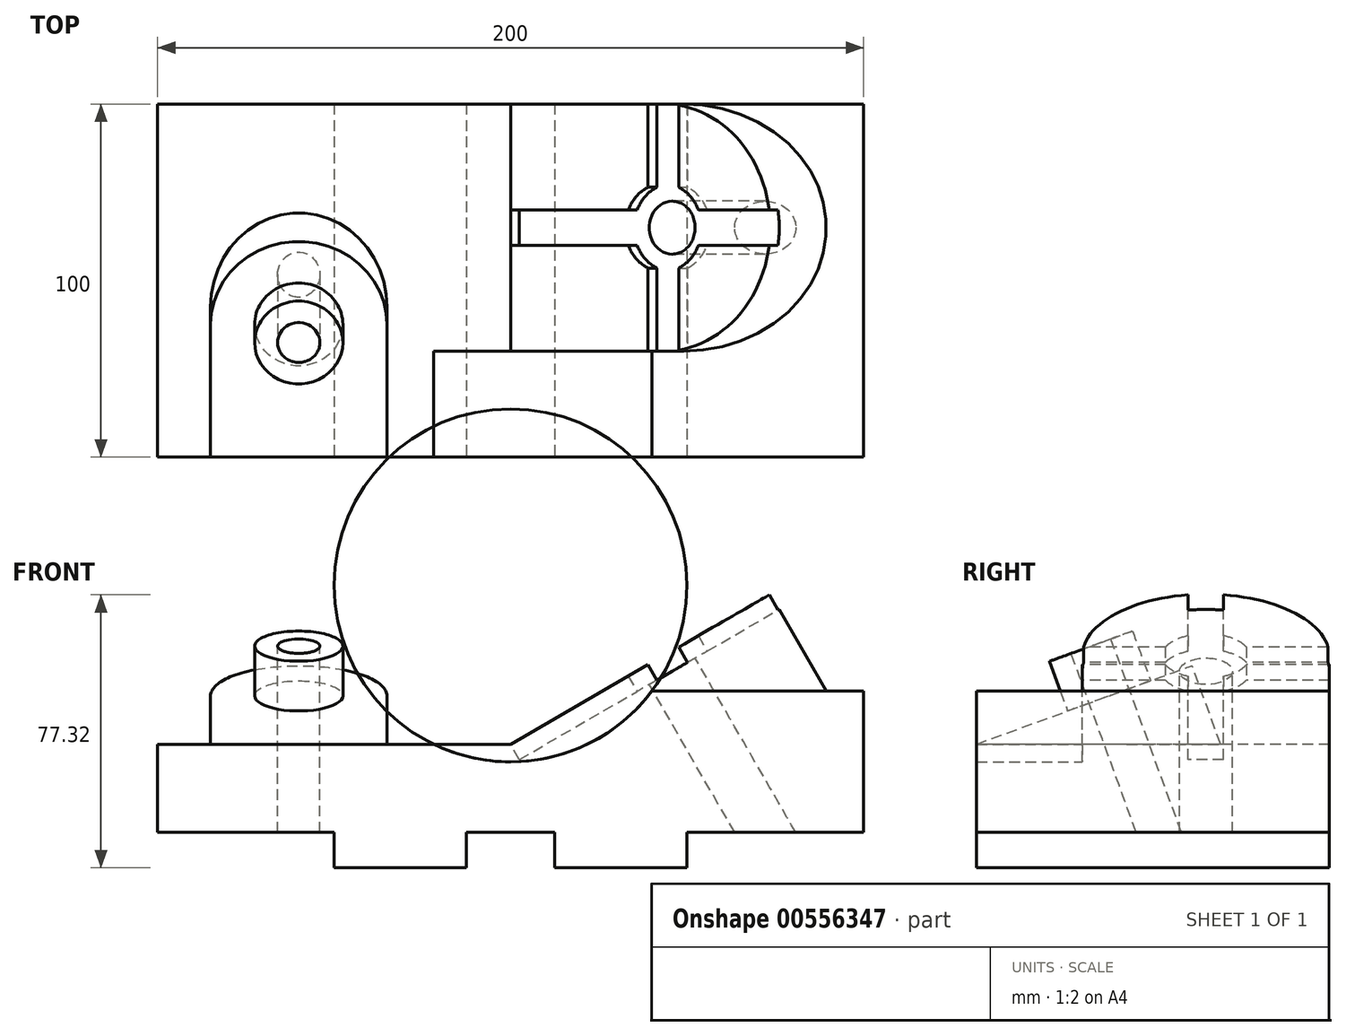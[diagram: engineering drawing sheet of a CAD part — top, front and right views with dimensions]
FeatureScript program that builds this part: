
annotation { "Feature Type Name" : "Feature", "Feature Type Description" : "" }
export const myFeature = defineFeature(function(context is Context, id is Id, definition is map)
    precondition{}
    {
        {
            var Q0;
            Q0=qCreatedBy(makeId("Front.planeOp"),FACE);
            var sketch = newSketch(context, id + "F0", { "sketchPlane" : qUnion([Q0])});
            skLineSegment(sketch, "E0", {"start": v(-200, 35) * mm, "end": v(-200, 10) * mm});
            skLineSegment(sketch, "E1", {"start": v(-200, 10) * mm, "end": v(-150, 10) * mm});
            skLineSegment(sketch, "E2", {"start": v(-150, 10) * mm, "end": v(-150, 0) * mm});
            skLineSegment(sketch, "E3", {"start": v(-150, 0) * mm, "end": v(-112.5, 0) * mm});
            skLineSegment(sketch, "E4", {"start": v(-112.5, 0) * mm, "end": v(-112.5, 10) * mm});
            skLineSegment(sketch, "E5", {"start": v(-112.5, 10) * mm, "end": v(-87.5, 10) * mm});
            skLineSegment(sketch, "E6", {"start": v(-87.5, 10) * mm, "end": v(-87.5, 0) * mm});
            skLineSegment(sketch, "E7", {"start": v(-87.5, 0) * mm, "end": v(-50, 0) * mm});
            skLineSegment(sketch, "E8", {"start": v(-50, 0) * mm, "end": v(-50, 10) * mm});
            skLineSegment(sketch, "E9", {"start": v(-50, 10) * mm, "end": v(0, 10) * mm});
            skLineSegment(sketch, "E10", {"start": v(0, 10) * mm, "end": v(0, 50) * mm});
            skLineSegment(sketch, "E11", {"start": v(-200, 35) * mm, "end": v(-100, 35) * mm});
            skLineSegment(sketch, "E12", {"start": v(-100, 35) * mm, "end": v(-60, 50) * mm});
            skLineSegment(sketch, "E13", {"start": v(-60, 50) * mm, "end": v(0, 50) * mm});
            skSolve(sketch);
        }
        {
            var Q0;
            Q0 = qSketchRegion(id + "F0", true);
            extrude(context, id + "F1", {"entities" : qUnion([Q0]), "oppositeDirection" : true, "depth" : 100 * mm, "offsetDistance" : 25 * mm});
        }
        {
            var Q0;
            Q0=makeQuery(id+"F1.opExtrude","CAP_EDGE",EDGE,{"disambiguationData":[OSD([sQuery(id+"F0.wireOp",EDGE,"E11")])],"isStart":true});
            var Q1;
            Q1=makeQuery(id+"F1.opExtrude","SWEPT_FACE",FACE,{"disambiguationData":[OSD([sQuery(id+"F0.wireOp",EDGE,"E11")])]});
            cPlane(context, id + "F2", {"entities" : qUnion([Q0, Q1]), "cplaneType" : CPlaneType.LINE_ANGLE, "offset" : 25 * mm, "angle" : 20 * degree, "width" : 150 * mm, "height" : 150 * mm});
        }
        {
            var Q0;
            Q0=qCreatedBy(id+"F2.planeOp",FACE);
            var sketch = newSketch(context, id + "F3", { "sketchPlane" : qUnion([Q0])});
            skLineSegment(sketch, "E14", {"start": v(-135, -11.97) * mm, "end": v(-135, -51.97) * mm});
            skLineSegment(sketch, "E15", {"start": v(-185, -51.97) * mm, "end": v(-185, -11.97) * mm});
            skLineSegment(sketch, "E16", {"start": v(-185, -11.97) * mm, "end": v(-135, -11.97) * mm});
            skArc(sketch, "E17", {"start": v(-135, -51.97) * mm, "mid": v(-160, -76.97) * mm, "end": v(-185, -51.97) * mm});
            skSolve(sketch);
        }
        {
            var Q0;
            Q0 = qSketchRegion(id + "F3", true);
            var Q1;
            Q1=makeQuery(id+"F1.opExtrude","SWEPT_BODY",BODY,{"disambiguationData":[OSD([sQuery(id+"F0.wireOp",EDGE,"E0"),sQuery(id+"F0.wireOp",EDGE,"E1"),sQuery(id+"F0.wireOp",EDGE,"E2"),sQuery(id+"F0.wireOp",EDGE,"E3"),sQuery(id+"F0.wireOp",EDGE,"E4"),sQuery(id+"F0.wireOp",EDGE,"E5"),sQuery(id+"F0.wireOp",EDGE,"E6"),sQuery(id+"F0.wireOp",EDGE,"E7"),sQuery(id+"F0.wireOp",EDGE,"E8"),sQuery(id+"F0.wireOp",EDGE,"E9"),sQuery(id+"F0.wireOp",EDGE,"E10"),sQuery(id+"F0.wireOp",EDGE,"E11"),sQuery(id+"F0.wireOp",EDGE,"E12"),sQuery(id+"F0.wireOp",EDGE,"E13")])]});
            extrude(context, id + "F4", {"entities" : qUnion([Q0]), "operationType" : NewBodyOperationType.ADD, "endBound" : BoundingType.UP_TO_BODY, "depth" : 25 * mm, "endBoundEntityBody" : qUnion([Q1]), "offsetDistance" : 25 * mm});
        }
        {
            var Q0;
            Q0=qCreatedBy(id+"F2.planeOp",FACE);
            var sketch = newSketch(context, id + "F5", { "sketchPlane" : qUnion([Q0])});
            skCircle(sketch, "E18", {"center": v(-160, -51.97) * mm, "radius": 12.5 * mm});
            skSolve(sketch);
        }
        {
            var Q0;
            Q0 = qSketchRegion(id + "F5", true);
            extrude(context, id + "F6", {"entities" : qUnion([Q0]), "operationType" : NewBodyOperationType.ADD, "oppositeDirection" : true, "depth" : 15 * mm, "offsetDistance" : 25 * mm});
        }
        {
            var Q0;
            Q0=makeQuery(id+"F6.opExtrude","CAP_FACE",FACE,{"disambiguationData":[OSD([sQuery(id+"F5.wireOp",EDGE,"E18")])],"isStart":false});
            var sketch = newSketch(context, id + "F7", { "sketchPlane" : qUnion([Q0])});
            skCircle(sketch, "E19", {"center": v(-160, 51.97) * mm, "radius": 6 * mm});
            skSolve(sketch);
        }
        {
            var Q0;
            Q0 = qSketchRegion(id + "F7", true);
            extrude(context, id + "F8", {"entities" : qUnion([Q0]), "operationType" : NewBodyOperationType.REMOVE, "endBound" : BoundingType.THROUGH_ALL, "oppositeDirection" : true, "depth" : 25 * mm, "offsetDistance" : 25 * mm});
        }
        {
            var Q0;
            Q0=makeQuery(id+"F1.opExtrude","SWEPT_EDGE",EDGE,{"disambiguationData":[OSD([sQuery(id+"F0.wireOp",EDGE,"E11"),sQuery(id+"F0.wireOp",EDGE,"E12")])]});
            var Q1;
            Q1=makeQuery(id+"F1.opExtrude","SWEPT_FACE",FACE,{"disambiguationData":[OSD([sQuery(id+"F0.wireOp",EDGE,"E11")])]});
            cPlane(context, id + "F9", {"entities" : qUnion([Q0, Q1]), "cplaneType" : CPlaneType.LINE_ANGLE, "offset" : 25 * mm, "angle" : 30 * degree, "width" : 150 * mm, "height" : 150 * mm});
        }
        {
            var Q0;
            Q0=qCreatedBy(id+"F9.planeOp",FACE);
            var sketch = newSketch(context, id + "F10", { "sketchPlane" : qUnion([Q0])});
            skLineSegment(sketch, "E20", {"start": v(-69.1, -30) * mm, "end": v(-69.1, -100) * mm});
            skLineSegment(sketch, "E21", {"start": v(-69.1, -100) * mm, "end": v(-19.1, -100) * mm});
            skArc(sketch, "E22", {"start": v(-19.1, -100) * mm, "mid": v(15.9, -65) * mm, "end": v(-19.1, -30) * mm});
            skLineSegment(sketch, "E23", {"start": v(-69.1, -30) * mm, "end": v(-19.1, -30) * mm});
            skSolve(sketch);
        }
        {
            var Q0;
            Q0 = qSketchRegion(id + "F10", true);
            var Q1;
            Q1=makeQuery(id+"F1.opExtrude","SWEPT_BODY",BODY,{"disambiguationData":[OSD([sQuery(id+"F0.wireOp",EDGE,"E0"),sQuery(id+"F0.wireOp",EDGE,"E1"),sQuery(id+"F0.wireOp",EDGE,"E2"),sQuery(id+"F0.wireOp",EDGE,"E3"),sQuery(id+"F0.wireOp",EDGE,"E4"),sQuery(id+"F0.wireOp",EDGE,"E5"),sQuery(id+"F0.wireOp",EDGE,"E6"),sQuery(id+"F0.wireOp",EDGE,"E7"),sQuery(id+"F0.wireOp",EDGE,"E8"),sQuery(id+"F0.wireOp",EDGE,"E9"),sQuery(id+"F0.wireOp",EDGE,"E10"),sQuery(id+"F0.wireOp",EDGE,"E11"),sQuery(id+"F0.wireOp",EDGE,"E12"),sQuery(id+"F0.wireOp",EDGE,"E13")])]});
            extrude(context, id + "F11", {"entities" : qUnion([Q0]), "operationType" : NewBodyOperationType.ADD, "endBound" : BoundingType.UP_TO_BODY, "depth" : 25 * mm, "endBoundEntityBody" : qUnion([Q1]), "offsetDistance" : 25 * mm});
        }
        {
            var Q0;
            Q0=makeQuery(id+"F11.opExtrude","SWEPT_FACE",FACE,{"disambiguationData":[OSD([sQuery(id+"F10.wireOp",EDGE,"E23")])]});
            var sketch = newSketch(context, id + "F12", { "sketchPlane" : qUnion([Q0])});
            skArc(sketch, "E24", {"start": v(-130.65, 40.5) * mm, "mid": v(-64.98, 44.31) * mm, "end": v(-59.92, 109.9) * mm});
            skLineSegment(sketch, "E25", {"start": v(-100, 80) * mm, "end": v(-100, 35) * mm, "construction": true});
            skLineSegment(sketch, "E26", {"start": v(-100, 35) * mm, "end": v(-100, 30) * mm, "construction": true});
            skLineSegment(sketch, "E27", {"start": v(-130.65, 40.5) * mm, "end": v(-59.92, 109.9) * mm});
            skSolve(sketch);
        }
        {
            var Q0;
            Q0 = qSketchRegion(id + "F12", true);
            extrude(context, id + "F13", {"entities" : qUnion([Q0]), "operationType" : NewBodyOperationType.REMOVE, "endBound" : BoundingType.THROUGH_ALL, "depth" : 25 * mm, "offsetDistance" : 25 * mm});
        }
        {
            var Q0;
            Q0=qCreatedBy(id+"F9.planeOp",FACE);
            var sketch = newSketch(context, id + "F14", { "sketchPlane" : qUnion([Q0])});
            skLineSegment(sketch, "E28.bottom", {"start": v(-24.1, -100) * mm, "end": v(-14.1, -100) * mm});
            skLineSegment(sketch, "E28.top", {"start": v(-24.1, -30) * mm, "end": v(-14.1, -30) * mm});
            skLineSegment(sketch, "E28.left", {"start": v(-24.1, -100) * mm, "end": v(-24.1, -70) * mm});
            skLineSegment(sketch, "E28.right", {"start": v(-14.1, -100) * mm, "end": v(-14.1, -70) * mm});
            skLineSegment(sketch, "E29.bottom", {"start": v(-69.1, -70) * mm, "end": v(-24.1, -70) * mm});
            skLineSegment(sketch, "E29.top", {"start": v(-69.1, -60) * mm, "end": v(-24.1, -60) * mm});
            skLineSegment(sketch, "E29.left", {"start": v(-69.1, -70) * mm, "end": v(-69.1, -60) * mm});
            skLineSegment(sketch, "E29.right", {"start": v(56.23, -70) * mm, "end": v(56.23, -60) * mm});
            skLineSegment(sketch, "E30.trimOffspring", {"start": v(-14.1, -70) * mm, "end": v(56.23, -70) * mm});
            skLineSegment(sketch, "E31.trimOffspring", {"start": v(-14.1, -60) * mm, "end": v(-14.1, -30) * mm});
            skLineSegment(sketch, "E32.trimOffspring", {"start": v(-14.1, -60) * mm, "end": v(56.23, -60) * mm});
            skLineSegment(sketch, "E33.trimOffspring", {"start": v(-24.1, -60) * mm, "end": v(-24.1, -30) * mm});
            skLineSegment(sketch, "E34", {"start": v(-14.1, -70) * mm, "end": v(-24.1, -60) * mm, "construction": true});
            skPoint(sketch, "E35", {"position": v(-19.1, -65) * mm});
            skSolve(sketch);
        }
        {
            var Q0;
            Q0=makeQuery(id+"F14.imprint","IMPRINT",FACE,{"disambiguationData":[TD([[makeQuery(id+"F14.imprint","IMPRINT",EDGE,{"derivedFrom":sQuery(id+"F14.wireOp",EDGE,"E28.bottom")}),1.0]])]});
            var Q1;
            Q1=sQuery(id+"F14.wireOp",EDGE,"E30.trimOffspring");
            extrude(context, id + "F15", {"entities" : qUnion([Q0]), "operationType" : NewBodyOperationType.REMOVE, "surfaceEntities" : qUnion([Q1]), "depth" : 5 * mm, "offsetDistance" : 25 * mm});
        }
        {
            var Q0;
            Q0=makeQuery(id+"F15.boolean.opBoolean","COPY",FACE,{"derivedFrom":makeQuery(id+"F15.opExtrude","CAP_FACE",FACE,{"disambiguationData":[OSD([sQuery(id+"F14.wireOp",EDGE,"E28.bottom"),sQuery(id+"F14.wireOp",EDGE,"E28.top"),sQuery(id+"F14.wireOp",EDGE,"E28.left"),sQuery(id+"F14.wireOp",EDGE,"E28.right"),sQuery(id+"F14.wireOp",EDGE,"E29.bottom"),sQuery(id+"F14.wireOp",EDGE,"E29.top"),sQuery(id+"F14.wireOp",EDGE,"E29.left"),sQuery(id+"F14.wireOp",EDGE,"E29.right"),sQuery(id+"F14.wireOp",EDGE,"E30.trimOffspring"),sQuery(id+"F14.wireOp",EDGE,"E31.trimOffspring"),sQuery(id+"F14.wireOp",EDGE,"E32.trimOffspring"),sQuery(id+"F14.wireOp",EDGE,"E33.trimOffspring")])],"isStart":false})});
            var sketch = newSketch(context, id + "F16", { "sketchPlane" : qUnion([Q0])});
            skCircle(sketch, "E36", {"center": v(-19.1, 65) * mm, "radius": 12.5 * mm});
            skSolve(sketch);
        }
        {
            var Q0;
            Q0 = qSketchRegion(id + "F16", true);
            extrude(context, id + "F17", {"entities" : qUnion([Q0]), "operationType" : NewBodyOperationType.REMOVE, "endBound" : BoundingType.THROUGH_ALL, "depth" : 25 * mm, "offsetDistance" : 25 * mm});
        }
        {
            var Q0;
            Q0=makeQuery(id+"F17.boolean.opBoolean","MERGE",FACE,{"derivedFrom":[makeQuery(id+"F15.boolean.opBoolean","COPY",FACE,{"derivedFrom":makeQuery(id+"F15.opExtrude","CAP_FACE",FACE,{"disambiguationData":[OSD([sQuery(id+"F14.wireOp",EDGE,"E28.bottom"),sQuery(id+"F14.wireOp",EDGE,"E28.top"),sQuery(id+"F14.wireOp",EDGE,"E28.left"),sQuery(id+"F14.wireOp",EDGE,"E28.right"),sQuery(id+"F14.wireOp",EDGE,"E29.bottom"),sQuery(id+"F14.wireOp",EDGE,"E29.top"),sQuery(id+"F14.wireOp",EDGE,"E29.left"),sQuery(id+"F14.wireOp",EDGE,"E29.right"),sQuery(id+"F14.wireOp",EDGE,"E30.trimOffspring"),sQuery(id+"F14.wireOp",EDGE,"E31.trimOffspring"),sQuery(id+"F14.wireOp",EDGE,"E32.trimOffspring"),sQuery(id+"F14.wireOp",EDGE,"E33.trimOffspring")])],"isStart":false})}),makeQuery(id+"F17.opExtrude","CAP_FACE",FACE,{"disambiguationData":[OSD([sQuery(id+"F16.wireOp",EDGE,"E36")])],"isStart":true})]});
            var sketch = newSketch(context, id + "F18", { "sketchPlane" : qUnion([Q0])});
            skCircle(sketch, "E37", {"center": v(-19.1, 65) * mm, "radius": 7.5 * mm});
            skSolve(sketch);
        }
        {
            var Q0;
            Q0 = qSketchRegion(id + "F18", true);
            extrude(context, id + "F19", {"entities" : qUnion([Q0]), "operationType" : NewBodyOperationType.REMOVE, "endBound" : BoundingType.THROUGH_ALL, "oppositeDirection" : true, "depth" : 25 * mm, "offsetDistance" : 25 * mm});
        }
        {
            var Q0;
            Q0=makeQuery(id+"F1.opExtrude","CAP_FACE",FACE,{"disambiguationData":[OSD([sQuery(id+"F0.wireOp",EDGE,"E0"),sQuery(id+"F0.wireOp",EDGE,"E1"),sQuery(id+"F0.wireOp",EDGE,"E2"),sQuery(id+"F0.wireOp",EDGE,"E3"),sQuery(id+"F0.wireOp",EDGE,"E4"),sQuery(id+"F0.wireOp",EDGE,"E5"),sQuery(id+"F0.wireOp",EDGE,"E6"),sQuery(id+"F0.wireOp",EDGE,"E7"),sQuery(id+"F0.wireOp",EDGE,"E8"),sQuery(id+"F0.wireOp",EDGE,"E9"),sQuery(id+"F0.wireOp",EDGE,"E10"),sQuery(id+"F0.wireOp",EDGE,"E11"),sQuery(id+"F0.wireOp",EDGE,"E12"),sQuery(id+"F0.wireOp",EDGE,"E13")])],"isStart":true});
            var sketch = newSketch(context, id + "F20", { "sketchPlane" : qUnion([Q0])});
            skLineSegment(sketch, "E38", {"start": v(-100, 30) * mm, "end": v(-100, 30) * mm});
            skSolve(sketch);
        }
        {
            var Q0;
            Q0 = qSketchRegion(id + "F20", true);
            extrude(context, id + "F21", {"entities" : qUnion([Q0]), "operationType" : NewBodyOperationType.REMOVE, "oppositeDirection" : true, "depth" : .1 * mm, "offsetDistance" : 25 * mm});
        }
    });
